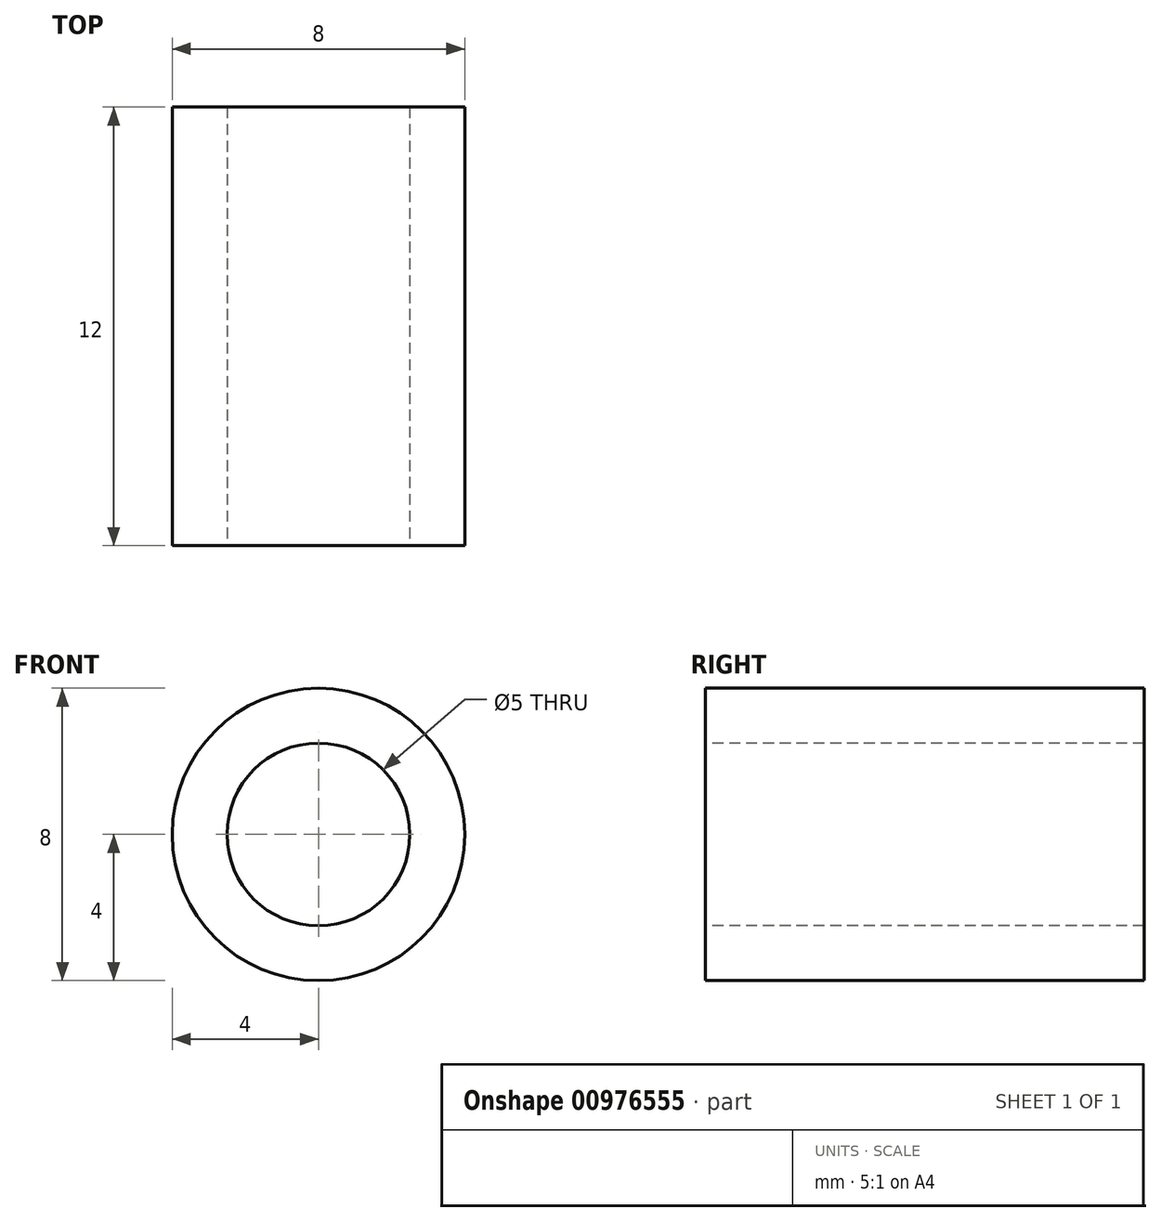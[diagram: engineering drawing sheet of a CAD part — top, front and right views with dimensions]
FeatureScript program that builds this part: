
annotation { "Feature Type Name" : "Feature", "Feature Type Description" : "" }
export const myFeature = defineFeature(function(context is Context, id is Id, definition is map)
    precondition{}
    {
        {
            var Q0;
            Q0=qCreatedBy(makeId("Front.planeOp"),FACE);
            var sketch = newSketch(context, id + "F0", { "sketchPlane" : qUnion([Q0])});
            skCircle(sketch, "E0", {"center": v(0, 0) * mm, "radius": 4 * mm});
            skSolve(sketch);
        }
        {
            var Q0;
            Q0=makeQuery(id+"F0.imprint","IMPRINT",FACE,{"disambiguationData":[TD([[makeQuery(id+"F0.imprint","IMPRINT",EDGE,{"derivedFrom":sQuery(id+"F0.wireOp",EDGE,"E0")}),1.0]])]});
            extrude(context, id + "F1", {"entities" : qUnion([Q0]), "endBound" : BoundingType.SYMMETRIC, "depth" : 12 * mm, "offsetDistance" : 25 * mm});
        }
        {
            var Q0;
            Q0=qCreatedBy(makeId("Front.planeOp"),FACE);
            var sketch = newSketch(context, id + "F2", { "sketchPlane" : qUnion([Q0])});
            skCircle(sketch, "E1", {"center": v(0, 0) * mm, "radius": 2.5 * mm});
            skSolve(sketch);
        }
        {
            var Q0;
            Q0 = qSketchRegion(id + "F2", true);
            extrude(context, id + "F3", {"entities" : qUnion([Q0]), "operationType" : NewBodyOperationType.REMOVE, "endBound" : BoundingType.SYMMETRIC, "oppositeDirection" : true, "depth" : 25 * mm, "offsetDistance" : 25 * mm});
        }
    });
